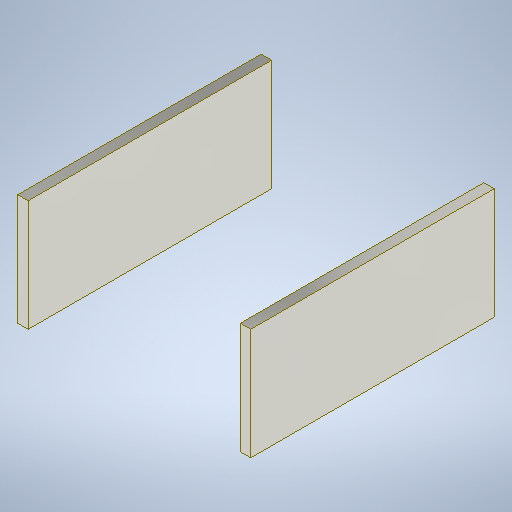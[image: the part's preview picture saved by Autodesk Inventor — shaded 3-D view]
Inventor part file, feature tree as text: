
AUTODESK INVENTOR PART (.ipt)
format: ipt  version: 2025.1 (Build 291241000, 241)  size: 218,112 bytes
history: native  units: mm
features: extrude x1, sketch x1
ambient origin geometry x8: Origin, YZ Plane, XZ Plane, XY Plane, X Axis, Y Axis, Z Axis, Center Point
bodies: Solid1 (feature_tree)
feature tree (2):
  extrude  "Extrusion1"  Depth=3.0mm
  sketch  "Sketch1"  dims[d0=67.0mm d1=3.0mm d2=32.0mm d3=16.0mm d5=0.0mm]
